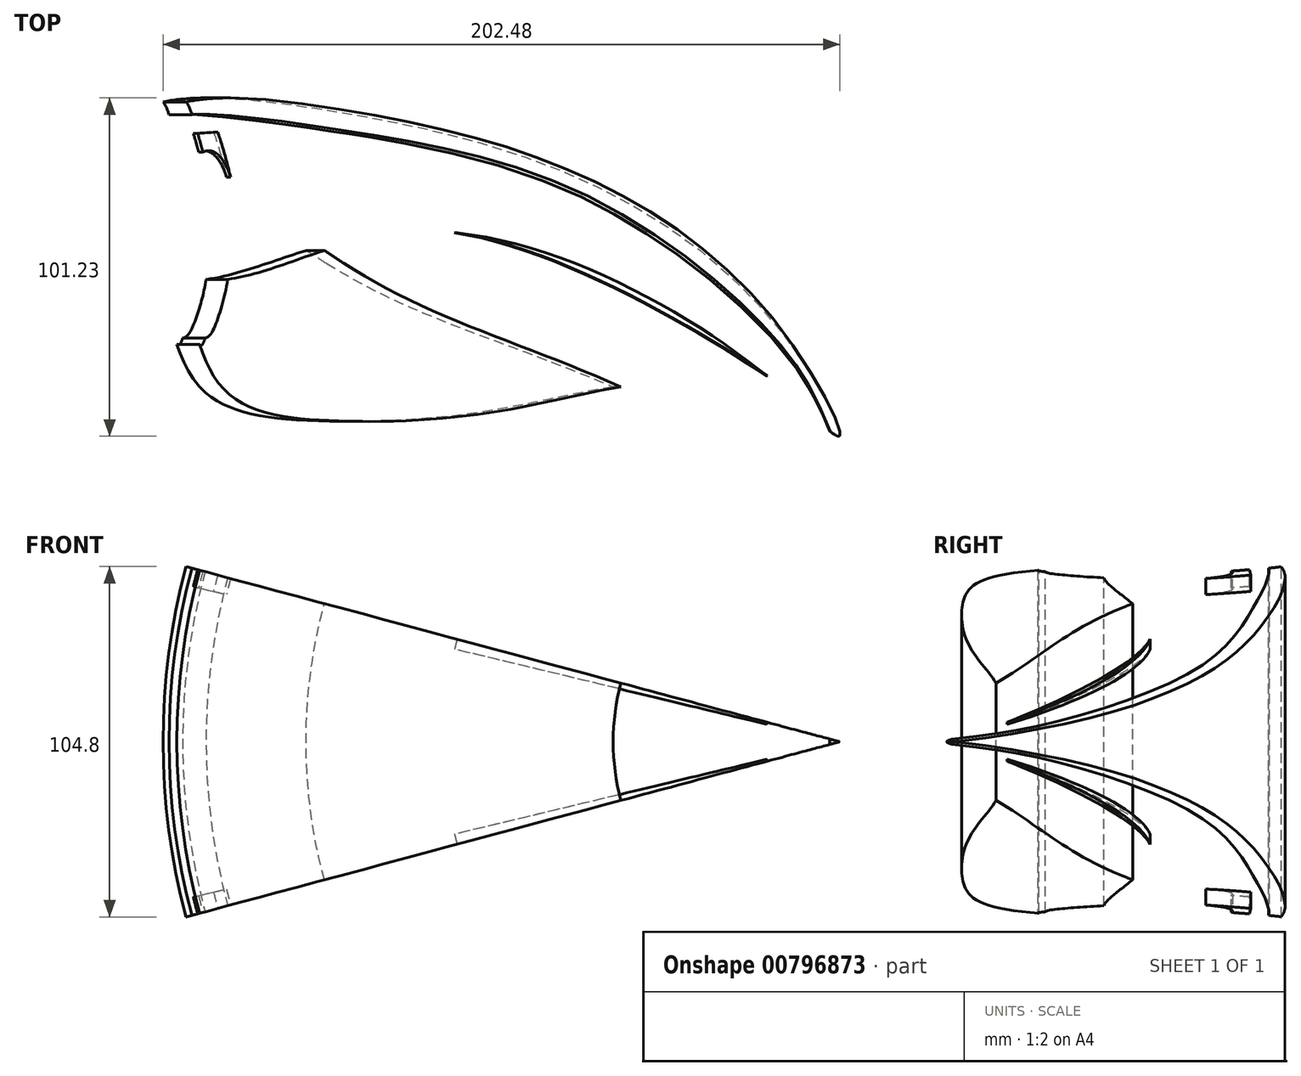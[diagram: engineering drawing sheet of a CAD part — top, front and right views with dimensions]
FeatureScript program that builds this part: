
annotation { "Feature Type Name" : "Feature", "Feature Type Description" : "" }
export const myFeature = defineFeature(function(context is Context, id is Id, definition is map)
    precondition{}
    {
        {
            var Q0;
            Q0=qCreatedBy(makeId("Top.planeOp"),FACE);
            var sketch = newSketch(context, id + "F0", { "sketchPlane" : qUnion([Q0])});
            skFitSpline(sketch, "E0", {"points": [v(-125.83, 74.2) * mm, v(-62.15, 80.76) * mm, v(13.7, 60.16) * mm, v(71.76, 17.09) * mm, v(91.42, -16.62) * mm, v(68.95, 1.17) * mm, v(-42.49, 44.24) * mm, v(-111.78, 32.07) * mm, v(-125.83, 74.2) * mm]});
            skLineSegment(sketch, "E1", {"start": v(-111.78, 32.07) * mm, "end": v(-111.78, 32.07) * mm});
            skLineSegment(sketch, "E2", {"start": v(-111.78, 74.2) * mm, "end": v(-111.78, 74.2) * mm});
            skFitSpline(sketch, "E3.trimOffspring", {"points": [v(-111.78, 32.07) * mm, v(-99.23, -2.95) * mm, v(-67.9, -12.11) * mm, v(-22.83, -10.58) * mm, v(10.78, -4.47) * mm, v(39.81, -1.42) * mm, v(68.84, -9.06) * mm, v(85.09, -12.54) * mm, v(68.95, 1.17) * mm, v(-42.49, 44.24) * mm, v(-83.95, 1.17) * mm], "startDerivative": vector(76.26, -423.63) * mm, "endDerivative": vector(-240.52, -486.65) * mm});
            skLineSegment(sketch, "E4", {"start": v(91.42, -16.62) * mm, "end": v(91.42, -37.76) * mm});
            skLineSegment(sketch, "E5", {"start": v(91.42, -16.62) * mm, "end": v(91.42, 24.2) * mm});
            skFitSpline(sketch, "E6", {"points": [v(-111.78, 83) * mm, v(-107.48, 73.73) * mm, v(-104.15, 59.75) * mm, v(-103.1, 40.47) * mm, v(-103.66, 21.27) * mm, v(-106.93, 10.66) * mm, v(-111.78, 83) * mm]});
            skFitSpline(sketch, "E7", {"points": [v(-103.72, 79.47) * mm, v(-63.47, 74.8) * mm, v(11.03, 56.1) * mm, v(69.74, 14.15) * mm, v(88.33, -15.28) * mm, v(93.89, -42.58) * mm, v(47.88, -14.46) * mm, v(-46.32, 26.04) * mm, v(-102.13, 64.75) * mm, v(-113.73, 77.64) * mm, v(-103.72, 79.47) * mm]});
            skFitSpline(sketch, "E8", {"points": [v(-103.72, 79.47) * mm, v(-101.26, 74.12) * mm, v(-97.02, 59.67) * mm], "startDerivative": vector(6.32, -12.06) * mm, "endDerivative": vector(7.04, -26.43) * mm});
            skFitSpline(sketch, "E9", {"points": [v(-97.02, 59.67) * mm, v(-97.02, 40.4) * mm, v(-98.63, 27.61) * mm, v(-101.46, 17.8) * mm, v(-103.99, 13.13) * mm, v(-106.94, 12.9) * mm, v(-118.61, 30.81) * mm, v(-116.97, 56.3) * mm, v(-114.73, 59.67) * mm, v(-104.47, 68.55) * mm, v(-97.02, 59.67) * mm]});
            skLineSegment(sketch, "E10", {"start": v(-107.48, 73.73) * mm, "end": v(-101.26, 74.12) * mm});
            skSolve(sketch);
        }
        {
            var Q0;
            {var subQ2=sQuery(id+"F0.wireOp",EDGE,"E3.trimOffspring");Q0=makeQuery(id+"F0.imprint","IMPRINT",FACE,{"disambiguationData":[TD([[makeQuery(id+"F0.imprint","IMPRINT",EDGE,{"derivedFrom":subQ2}),-1.0]])]});}
            var Q1;
            {var subQ4=sQuery(id+"F0.wireOp",EDGE,"E10");Q1=makeQuery(id+"F0.imprint","IMPRINT",FACE,{"disambiguationData":[TD([[makeQuery(id+"F0.imprint","IMPRINT",EDGE,{"derivedFrom":subQ4}),-1.0]])]});}
            var Q2;
            {var subQ4=sQuery(id+"F0.wireOp",EDGE,"E7");Q2=makeQuery(id+"F0.imprint","IMPRINT",FACE,{"disambiguationData":[TD([[makeQuery(id+"F0.imprint","IMPRINT",EDGE,{"derivedFrom":subQ4}),1.0]])]});}
            var Q3;
            Q3=sQuery(id+"F0.wireOp",EDGE,"E4");
            revolve(context, id + "F1", {"surfaceOperationType" : NewSurfaceOperationType.NEW, "entities" : qUnion([Q0, Q1, Q2]), "axis" : qUnion([Q3]), "revolveType" : RevolveType.SYMMETRIC, "angle" : 30 * degree});
        }
        {
            var Q0;
            {var subQ1=sQuery(id+"F0.wireOp",EDGE,"E3.trimOffspring");Q0=makeQuery(id+"F0.imprint","IMPRINT",FACE,{"disambiguationData":[TD([[makeQuery(id+"F0.imprint","IMPRINT",EDGE,{"derivedFrom":subQ1}),-1.0]])]});}
            var Q1;
            {var subQ4=sQuery(id+"F0.wireOp",EDGE,"E10");Q1=makeQuery(id+"F0.imprint","IMPRINT",FACE,{"disambiguationData":[TD([[makeQuery(id+"F0.imprint","IMPRINT",EDGE,{"derivedFrom":subQ4}),-1.0]])]});}
            var Q2;
            Q2=sQuery(id+"F0.wireOp",EDGE,"E5");
            revolve(context, id + "F2", {"operationType" : NewBodyOperationType.REMOVE, "surfaceOperationType" : NewSurfaceOperationType.NEW, "entities" : qUnion([Q0, Q1]), "axis" : qUnion([Q2]), "revolveType" : RevolveType.SYMMETRIC, "oppositeDirection" : true, "angle" : 27 * degree});
        }
    });
